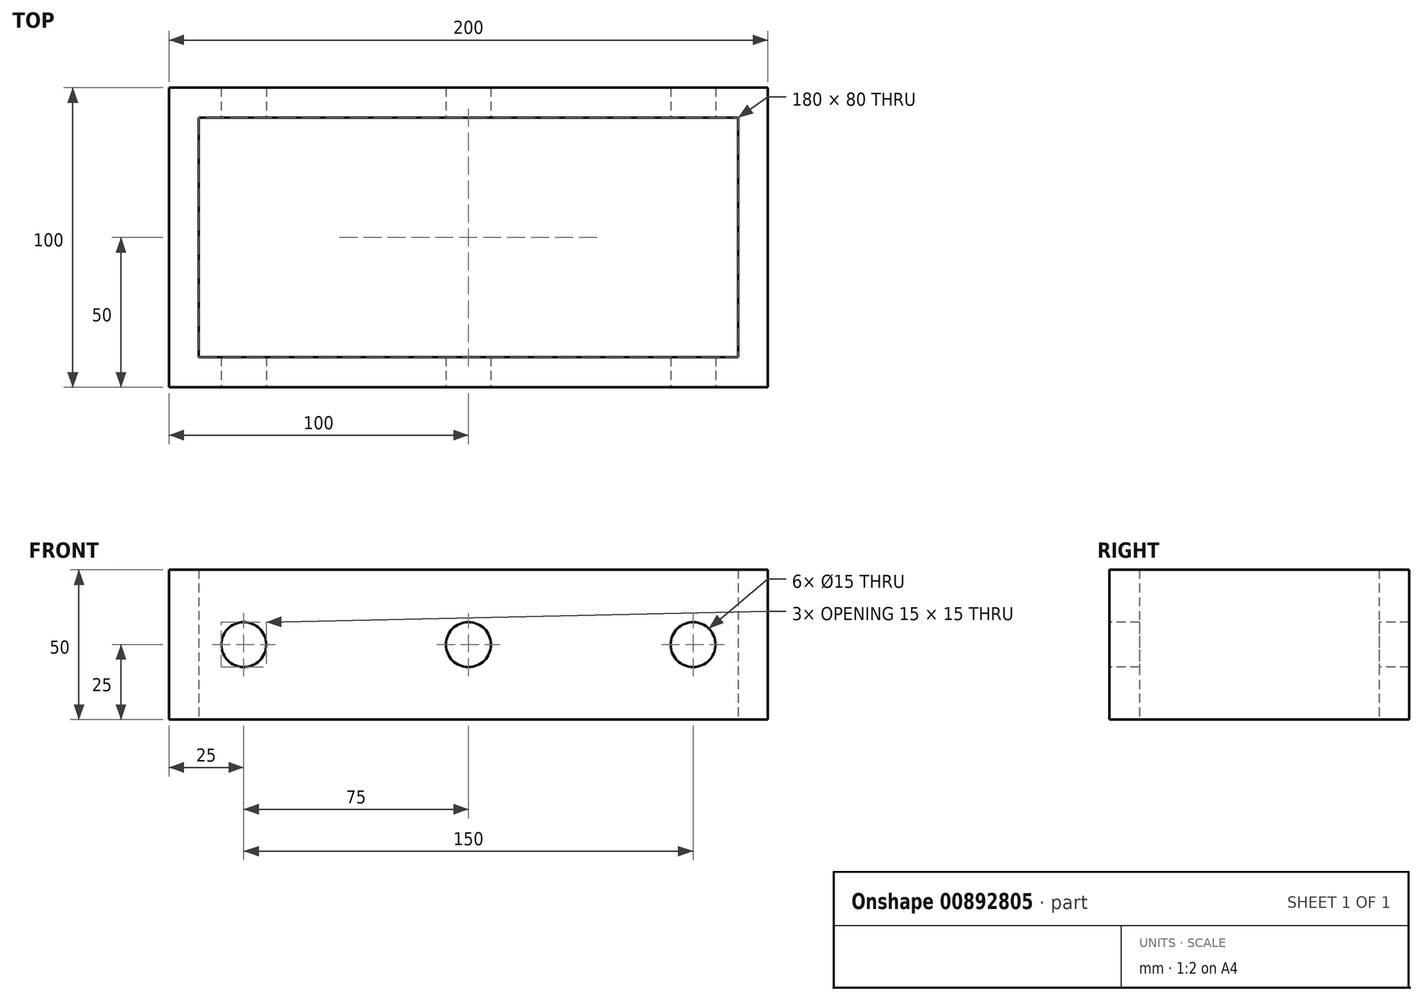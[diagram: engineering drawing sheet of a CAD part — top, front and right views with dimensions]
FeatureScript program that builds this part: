
annotation { "Feature Type Name" : "Feature", "Feature Type Description" : "" }
export const myFeature = defineFeature(function(context is Context, id is Id, definition is map)
    precondition{}
    {
        {
            var Q0;
            Q0=qCreatedBy(makeId("Top.planeOp"),FACE);
            var sketch = newSketch(context, id + "F0", { "sketchPlane" : qUnion([Q0])});
            skLineSegment(sketch, "E0.bottom", {"start": v(-100, 50) * mm, "end": v(100, 50) * mm});
            skLineSegment(sketch, "E0.top", {"start": v(-100, -50) * mm, "end": v(100, -50) * mm});
            skLineSegment(sketch, "E0.left", {"start": v(-100, 50) * mm, "end": v(-100, -50) * mm});
            skLineSegment(sketch, "E0.right", {"start": v(100, 50) * mm, "end": v(100, -50) * mm});
            skLineSegment(sketch, "E1.bottom", {"start": v(-90, 40) * mm, "end": v(90, 40) * mm});
            skLineSegment(sketch, "E1.top", {"start": v(-90, -40) * mm, "end": v(90, -40) * mm});
            skLineSegment(sketch, "E1.left", {"start": v(-90, 40) * mm, "end": v(-90, -40) * mm});
            skLineSegment(sketch, "E1.right", {"start": v(90, 40) * mm, "end": v(90, -40) * mm});
            skSolve(sketch);
        }
        {
            var Q0;
            Q0 = qSketchRegion(id + "F0", true);
            extrude(context, id + "F1", {"entities" : qUnion([Q0]), "depth" : 50 * mm, "offsetDistance" : 25 * mm});
        }
        {
            var Q0;
            Q0=qCreatedBy(makeId("Front.planeOp"),FACE);
            var sketch = newSketch(context, id + "F2", { "sketchPlane" : qUnion([Q0])});
            skCircle(sketch, "E2", {"center": v(0, 25) * mm, "radius": 7.5 * mm});
            skCircle(sketch, "E3", {"center": v(-75, 25) * mm, "radius": 7.5 * mm});
            skCircle(sketch, "E4", {"center": v(75, 25) * mm, "radius": 7.5 * mm});
            skSolve(sketch);
        }
        {
            var Q0;
            Q0 = qSketchRegion(id + "F2", true);
            extrude(context, id + "F3", {"entities" : qUnion([Q0]), "operationType" : NewBodyOperationType.REMOVE, "endBound" : BoundingType.SYMMETRIC, "oppositeDirection" : true, "depth" : 100 * mm, "offsetDistance" : 25 * mm});
        }
    });
